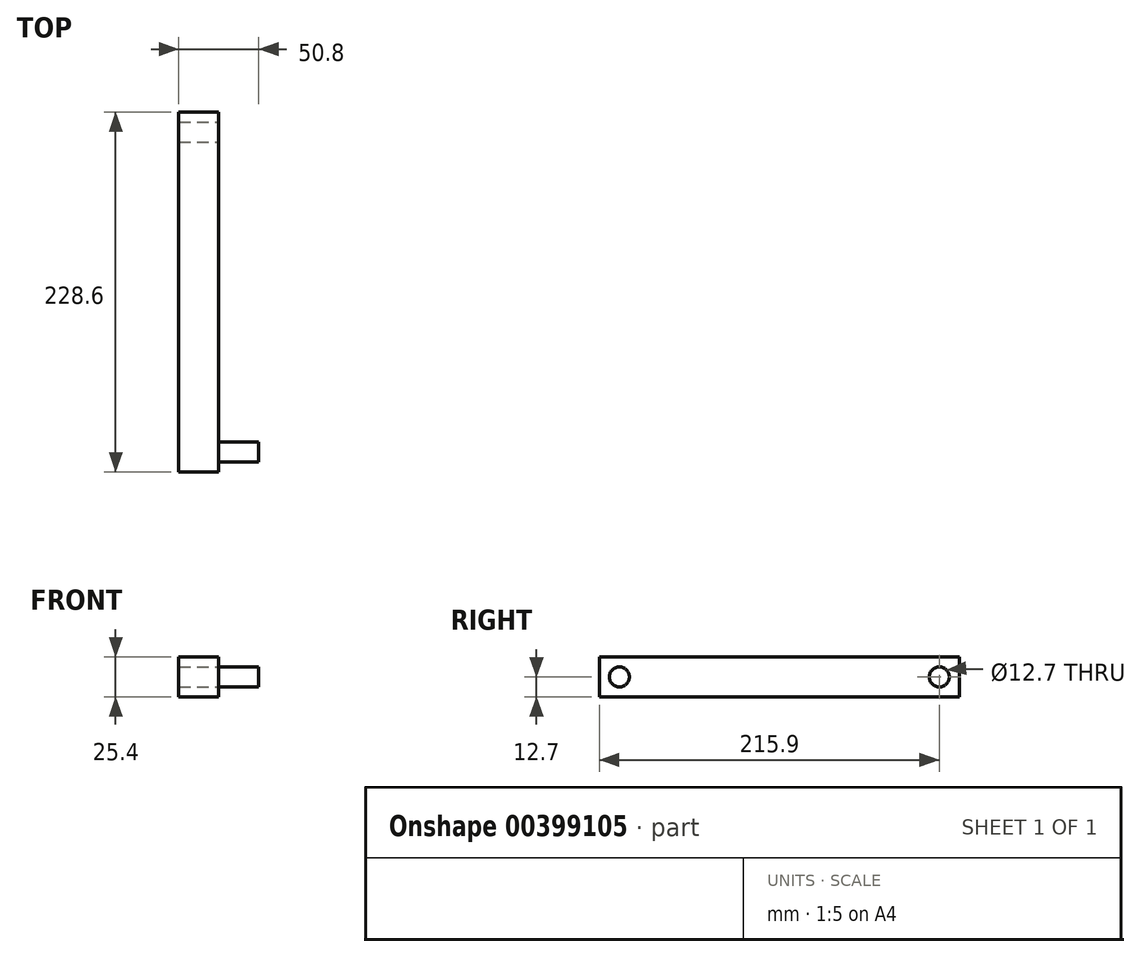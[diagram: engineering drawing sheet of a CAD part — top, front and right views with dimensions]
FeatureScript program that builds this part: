
annotation { "Feature Type Name" : "Feature", "Feature Type Description" : "" }
export const myFeature = defineFeature(function(context is Context, id is Id, definition is map)
    precondition{}
    {
        {
            var Q0;
            Q0=qCreatedBy(makeId("Right.planeOp"),FACE);
            var sketch = newSketch(context, id + "F0", { "sketchPlane" : qUnion([Q0])});
            skLineSegment(sketch, "E0.bottom", {"start": v(114.3, 12.7) * mm, "end": v(-114.3, 12.7) * mm});
            skLineSegment(sketch, "E0.top", {"start": v(114.3, -12.7) * mm, "end": v(-114.3, -12.7) * mm});
            skLineSegment(sketch, "E0.left", {"start": v(114.3, 12.7) * mm, "end": v(114.3, -12.7) * mm});
            skLineSegment(sketch, "E0.right", {"start": v(-114.3, 12.7) * mm, "end": v(-114.3, -12.7) * mm});
            skPoint(sketch, "E0.middle", {"position": v(0, 0) * mm});
            skSolve(sketch);
        }
        {
            var Q0;
            Q0=makeQuery(id+"F0.imprint","IMPRINT",FACE,{"disambiguationData":[TD([[makeQuery(id+"F0.imprint","IMPRINT",EDGE,{"derivedFrom":sQuery(id+"F0.wireOp",EDGE,"E0.bottom")}),1.0]])]});
            extrude(context, id + "F1", {"entities" : qUnion([Q0]), "depth" : 25.4 * mm});
        }
        {
            var Q0;
            Q0=makeQuery(id+"F1.opExtrude","CAP_FACE",FACE,{"disambiguationData":[OSD([sQuery(id+"F0.wireOp",EDGE,"E0.bottom"),sQuery(id+"F0.wireOp",EDGE,"E0.top"),sQuery(id+"F0.wireOp",EDGE,"E0.left"),sQuery(id+"F0.wireOp",EDGE,"E0.right")])],"isStart":false});
            var sketch = newSketch(context, id + "F2", { "sketchPlane" : qUnion([Q0])});
            skCircle(sketch, "E1", {"center": v(-101.6, 0) * mm, "radius": 6.35 * mm});
            skSolve(sketch);
        }
        {
            var Q0;
            Q0=makeQuery(id+"F2.imprint","IMPRINT",FACE,{"disambiguationData":[TD([[makeQuery(id+"F2.imprint","IMPRINT",EDGE,{"derivedFrom":sQuery(id+"F2.wireOp",EDGE,"E1")}),1.0]])]});
            extrude(context, id + "F3", {"entities" : qUnion([Q0]), "operationType" : NewBodyOperationType.ADD, "depth" : 25.4 * mm});
        }
        {
            var Q0;
            Q0=makeQuery(id+"F1.opExtrude","CAP_FACE",FACE,{"disambiguationData":[OSD([sQuery(id+"F0.wireOp",EDGE,"E0.bottom"),sQuery(id+"F0.wireOp",EDGE,"E0.top"),sQuery(id+"F0.wireOp",EDGE,"E0.left"),sQuery(id+"F0.wireOp",EDGE,"E0.right")])],"isStart":false});
            var sketch = newSketch(context, id + "F4", { "sketchPlane" : qUnion([Q0])});
            skCircle(sketch, "E2", {"center": v(101.6, 0) * mm, "radius": 6.35 * mm});
            skSolve(sketch);
        }
        {
            var Q0;
            Q0=makeQuery(id+"F4.imprint","IMPRINT",FACE,{"disambiguationData":[TD([[makeQuery(id+"F4.imprint","IMPRINT",EDGE,{"derivedFrom":sQuery(id+"F4.wireOp",EDGE,"E2")}),1.0]])]});
            extrude(context, id + "F5", {"entities" : qUnion([Q0]), "operationType" : NewBodyOperationType.REMOVE, "oppositeDirection" : true, "depth" : 25.4 * mm});
        }
    });
